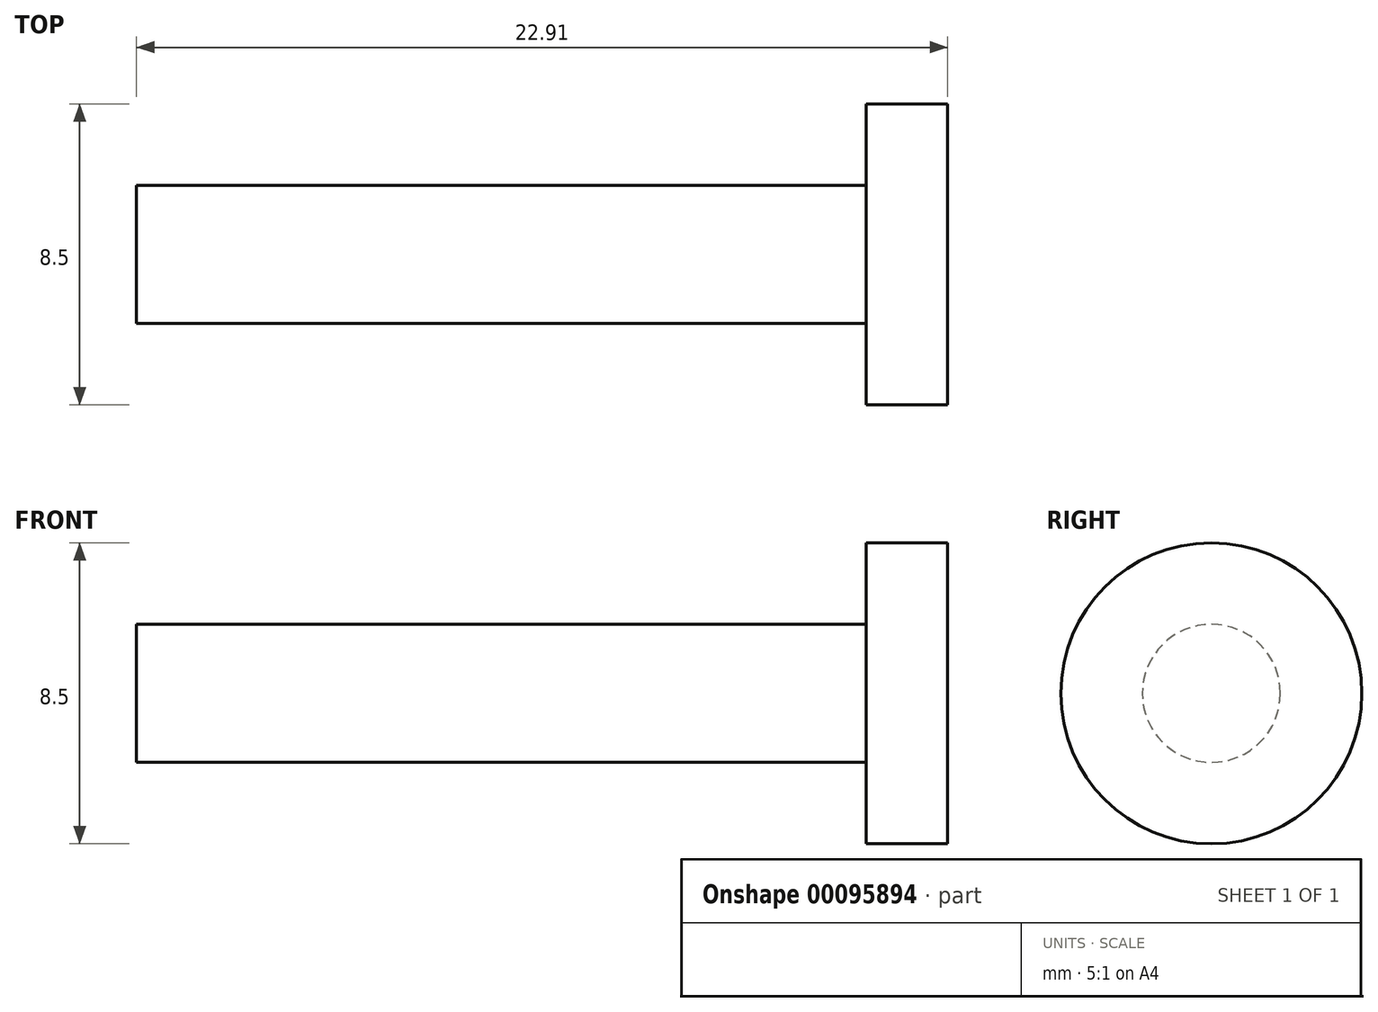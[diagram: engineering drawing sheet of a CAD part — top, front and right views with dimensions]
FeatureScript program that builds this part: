
annotation { "Feature Type Name" : "Feature", "Feature Type Description" : "" }
export const myFeature = defineFeature(function(context is Context, id is Id, definition is map)
    precondition{}
    {
        {
            var Q0;
            Q0=qCreatedBy(makeId("Front.planeOp"),FACE);
            var sketch = newSketch(context, id + "F0", { "sketchPlane" : qUnion([Q0])});
            skLineSegment(sketch, "E0", {"start": v(0, 0) * mm, "end": v(-22.9, 0) * mm});
            skLineSegment(sketch, "E1", {"start": v(-22.9, 0) * mm, "end": v(-22.9, 1.95) * mm});
            skLineSegment(sketch, "E2", {"start": v(-22.9, 1.95) * mm, "end": v(-2.3, 1.95) * mm});
            skLineSegment(sketch, "E3", {"start": v(-2.3, 1.95) * mm, "end": v(-2.3, 4.25) * mm});
            skLineSegment(sketch, "E4", {"start": v(-2.3, 4.25) * mm, "end": v(0, 4.25) * mm});
            skLineSegment(sketch, "E5", {"start": v(0, 4.25) * mm, "end": v(0, 0) * mm});
            skSolve(sketch);
        }
        {
            var Q0;
            Q0=makeQuery(id+"F0.imprint","IMPRINT",FACE,{"disambiguationData":[TD([[makeQuery(id+"F0.imprint","IMPRINT",EDGE,{"derivedFrom":sQuery(id+"F0.wireOp",EDGE,"E0")}),-1.0]])]});
            var Q1;
            Q1=sQuery(id+"F0.wireOp",EDGE,"E0");
            revolve(context, id + "F1", {"entities" : qUnion([Q0]), "axis" : qUnion([Q1]), "revolveType" : RevolveType.FULL});
        }
    });
